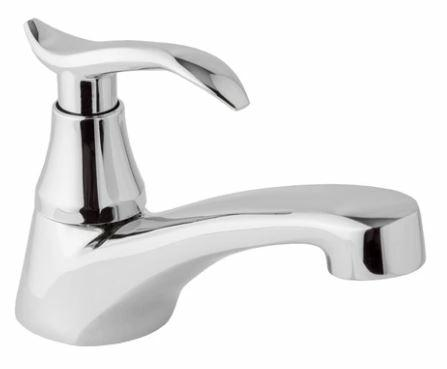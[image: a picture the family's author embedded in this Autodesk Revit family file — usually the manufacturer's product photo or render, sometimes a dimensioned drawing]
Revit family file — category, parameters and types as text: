
# Revit family: 01-18152-11P LLAVE INDIVIDUAL LAVATORIO BRONCE TEDESCA
name_source: partatom
category: Plumbing Fixtures
revit_build: Autodesk Revit 2018 (Build: 20170223_1515(x64)
units: mm (PartAtom-declared; Revit-internal decimal feet)

## family parameters
Cut with Voids When Loaded = No
Host = Face
OmniClass Number = 23.31.11.00
Part Type = Normal
Room Calculation Point = No
Round Connector Dimension = Use Diameter
Shared = No

## types (1)
- 01-18152-11P
    Alto = 80.2 mm  [stored 0.263123 ft]
    Ancho a aireador = 105 mm  [stored 0.344488 ft]
    CW Connection = Yes
    Default Elevation = 0 mm  [stored 0 ft]
    Description = Llave individual
    Dim base = 46 mm  [stored 0.150919 ft]
    HW Connection = Yes
    Link Ficha Tecnica = http://infotecnica.gricol.com
    Manija = 80 mm
    Manufacturer = Gricol
    Metal Laton Cromado = Metal Laton Cromado
    Model = 01-18152-11P
    Plastico ABS Cromado = Plastico - ABS Cromado
    Product Name = LLAVE INDIVIDUAL LAVATORIO BRONCE TEDESCA
    Type Image = LLAVE INDIVIDUAL LAVATORIO BRONCE TEDESCA.JPG
    URL = https://www.gricol.com
    Vent Connection = No
    Waste Connection = No

note: [stored X ft] marks values corroborated as IEEE doubles in the binary element streams (Revit-internal decimal feet)

## geometry (parser evidence)
native form markers: Blend x2, Sweep x2
no freeform markers — native parametric forms only
